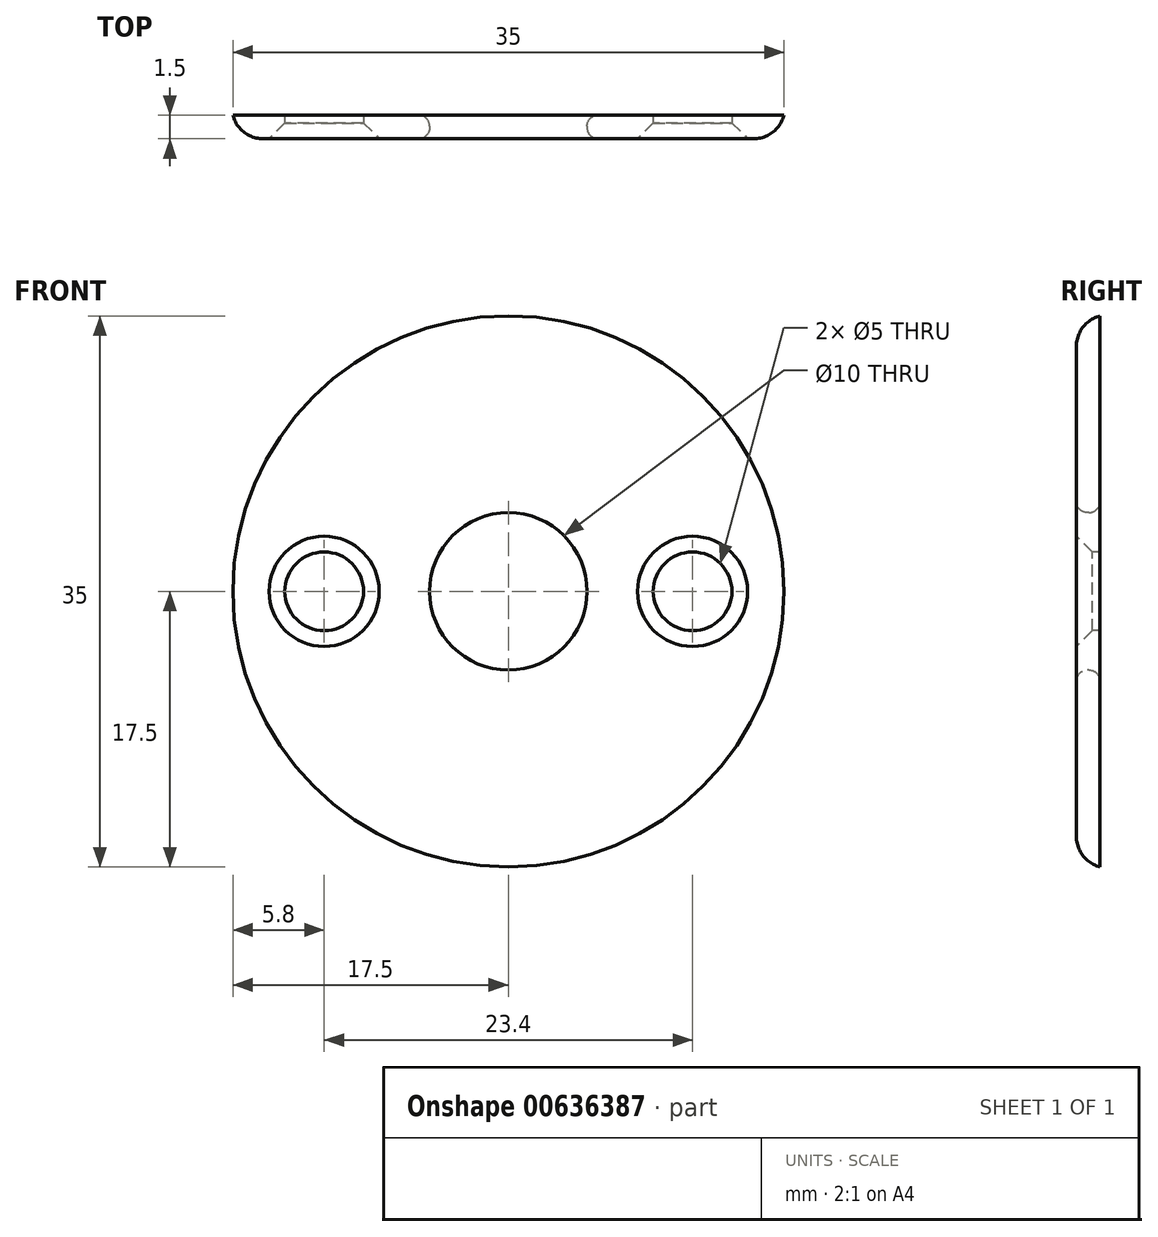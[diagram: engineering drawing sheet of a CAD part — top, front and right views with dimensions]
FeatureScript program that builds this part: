
annotation { "Feature Type Name" : "Feature", "Feature Type Description" : "" }
export const myFeature = defineFeature(function(context is Context, id is Id, definition is map)
    precondition{}
    {
        {
            var Q0;
            Q0=qCreatedBy(makeId("Front.planeOp"),FACE);
            var sketch = newSketch(context, id + "F0", { "sketchPlane" : qUnion([Q0])});
            skCircle(sketch, "E0", {"center": v(0, 0) * mm, "radius": 17.5 * mm});
            skCircle(sketch, "E1", {"center": v(0, 0) * mm, "radius": 5 * mm});
            skPoint(sketch, "E2", {"position": v(11.7, 0) * mm});
            skPoint(sketch, "E3", {"position": v(-11.7, 0) * mm});
            skSolve(sketch);
        }
        {
            var Q0;
            Q0=makeQuery(id+"F0.imprint","IMPRINT",FACE,{"disambiguationData":[TD([[makeQuery(id+"F0.imprint","IMPRINT",EDGE,{"derivedFrom":sQuery(id+"F0.wireOp",EDGE,"E0")}),1.0]])]});
            extrude(context, id + "F1", {"entities" : qUnion([Q0]), "oppositeDirection" : true, "depth" : 1.5 * mm, "offsetDistance" : 25 * mm});
        }
        {
            var Q0;
            Q0=sQuery(id+"F0.wireOp",VERTEX,"E3");
            var Q1;
            Q1=sQuery(id+"F0.wireOp",VERTEX,"E2");
            var Q2;
            Q2=makeQuery(id+"F1.opExtrude","SWEPT_BODY",BODY,{"disambiguationData":[OSD([sQuery(id+"F0.wireOp",EDGE,"E0"),sQuery(id+"F0.wireOp",EDGE,"E1")])]});
            hole(context, id + "F2", {"style" : HoleStyle.C_SINK, "endStyle" : HoleEndStyle.THROUGH, "holeDiameter" : 5 * mm, "cSinkDiameter" : 7 * mm, "cSinkAngle" : 90 * degree, "majorDiameter" : 5 * mm, "isTappedThrough" : true, "tappedDepth" : 12 * mm, "tapClearance" : 3, "startFromSketch" : true, "locations" : qUnion([Q0, Q1]), "scope" : qUnion([Q2])});
        }
        {
            var Q0;
            Q0=makeQuery(id+"F1.opExtrude","CAP_EDGE",EDGE,{"disambiguationData":[OSD([sQuery(id+"F0.wireOp",EDGE,"E0")])],"isStart":true});
            fillet(context, id + "F3", {"entities" : qUnion([Q0]), "radius" : 2 * mm, "allowEdgeOverflow" : false});
        }
        {
            var Q0;
            Q0=makeQuery(id+"F1.opExtrude","CAP_EDGE",EDGE,{"disambiguationData":[OSD([sQuery(id+"F0.wireOp",EDGE,"E1")])],"isStart":true});
            var Q1;
            Q1=makeQuery(id+"F1.opExtrude","CAP_EDGE",EDGE,{"disambiguationData":[OSD([sQuery(id+"F0.wireOp",EDGE,"E1")])],"isStart":false});
            fillet(context, id + "F4", {"entities" : qUnion([Q0, Q1]), "radius" : 0.7 * mm, "allowEdgeOverflow" : false});
        }
    });
